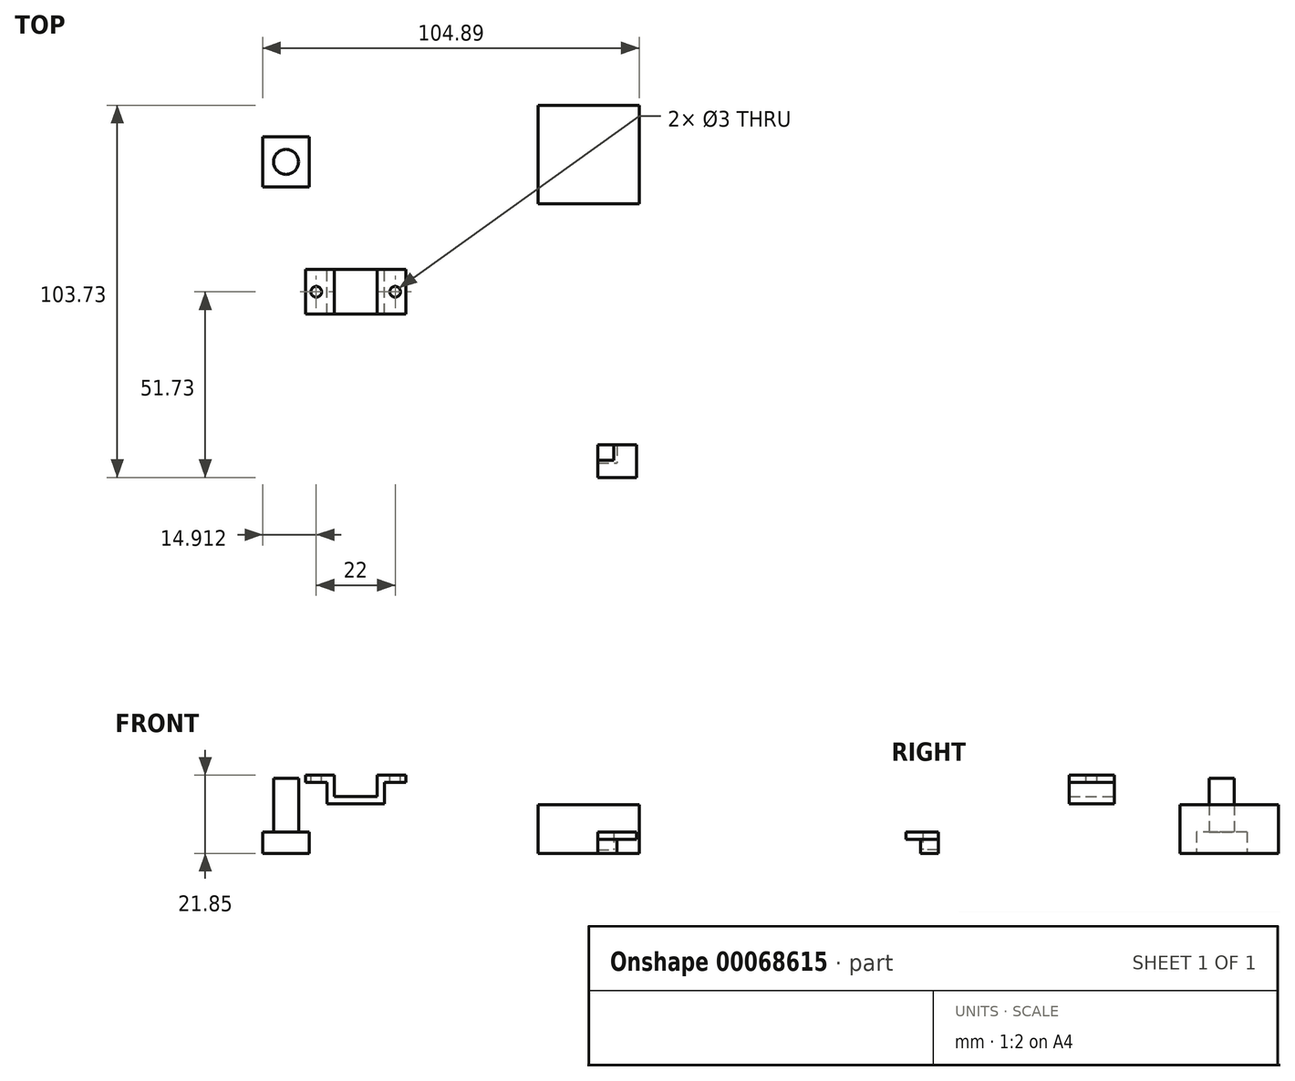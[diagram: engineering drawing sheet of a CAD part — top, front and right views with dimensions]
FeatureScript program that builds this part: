
annotation { "Feature Type Name" : "Feature", "Feature Type Description" : "" }
export const myFeature = defineFeature(function(context is Context, id is Id, definition is map)
    precondition{}
    {
        {
            var Q0;
            Q0=qCreatedBy(makeId("Front.planeOp"),FACE);
            var sketch = newSketch(context, id + "F0", { "sketchPlane" : qUnion([Q0])});
            skLineSegment(sketch, "E0", {"start": v(-31.6, 15.85) * mm, "end": v(-19.6, 15.85) * mm});
            skLineSegment(sketch, "E1", {"start": v(-19.6, 15.85) * mm, "end": v(-19.6, 21.85) * mm});
            skLineSegment(sketch, "E2", {"start": v(-19.6, 21.85) * mm, "end": v(-11.6, 21.85) * mm});
            skLineSegment(sketch, "E3", {"start": v(-11.6, 21.85) * mm, "end": v(-11.6, 19.85) * mm});
            skLineSegment(sketch, "E4", {"start": v(-11.6, 19.85) * mm, "end": v(-17.6, 19.85) * mm});
            skLineSegment(sketch, "E5", {"start": v(-17.6, 19.85) * mm, "end": v(-17.6, 13.85) * mm});
            skLineSegment(sketch, "E6", {"start": v(-17.6, 13.85) * mm, "end": v(-33.6, 13.85) * mm});
            skLineSegment(sketch, "E7", {"start": v(-33.6, 13.85) * mm, "end": v(-33.6, 19.85) * mm});
            skLineSegment(sketch, "E8", {"start": v(-33.6, 19.85) * mm, "end": v(-39.6, 19.85) * mm});
            skLineSegment(sketch, "E9", {"start": v(-39.6, 19.85) * mm, "end": v(-39.6, 21.85) * mm});
            skLineSegment(sketch, "E10", {"start": v(-39.6, 21.85) * mm, "end": v(-31.6, 21.85) * mm});
            skLineSegment(sketch, "E11", {"start": v(-31.6, 21.85) * mm, "end": v(-31.6, 15.85) * mm});
            skSolve(sketch);
        }
        {
            var Q0;
            Q0 = qSketchRegion(id + "F0", true);
            extrude(context, id + "F1", {"entities" : qUnion([Q0]), "depth" : 12.5 * mm});
        }
        {
            var Q0;
            Q0=makeQuery(id+"F1.opExtrude","CAP_FACE",FACE,{"disambiguationData":[OSD([sQuery(id+"F0.wireOp",EDGE,"E0"),sQuery(id+"F0.wireOp",EDGE,"E1"),sQuery(id+"F0.wireOp",EDGE,"E2"),sQuery(id+"F0.wireOp",EDGE,"E3"),sQuery(id+"F0.wireOp",EDGE,"E4"),sQuery(id+"F0.wireOp",EDGE,"E5"),sQuery(id+"F0.wireOp",EDGE,"E6"),sQuery(id+"F0.wireOp",EDGE,"E7"),sQuery(id+"F0.wireOp",EDGE,"E8"),sQuery(id+"F0.wireOp",EDGE,"E9"),sQuery(id+"F0.wireOp",EDGE,"E10"),sQuery(id+"F0.wireOp",EDGE,"E11")])],"isStart":false});
            cPlane(context, id + "F2", {"entities" : qUnion([Q0]), "cplaneType" : CPlaneType.OFFSET, "offset" : 2 * mm, "width" : 150 * mm, "height" : 150 * mm});
        }
        {
            var Q0;
            Q0=makeQuery(id+"F1.opExtrude","SWEPT_FACE",FACE,{"disambiguationData":[OSD([sQuery(id+"F0.wireOp",EDGE,"E10")])]});
            var sketch = newSketch(context, id + "F3", { "sketchPlane" : qUnion([Q0])});
            skCircle(sketch, "E12", {"center": v(-36.6, -6.25) * mm, "radius": 1.5 * mm});
            skCircle(sketch, "E13", {"center": v(-14.6, -6.25) * mm, "radius": 1.5 * mm});
            skSolve(sketch);
        }
        {
            var Q0;
            Q0 = qSketchRegion(id + "F3", true);
            extrude(context, id + "F4", {"entities" : qUnion([Q0]), "operationType" : NewBodyOperationType.REMOVE, "oppositeDirection" : true, "depth" : 2 * mm});
        }
        {
            var Q0;
            Q0=qCreatedBy(makeId("Top.planeOp"),FACE);
            var sketch = newSketch(context, id + "F5", { "sketchPlane" : qUnion([Q0])});
            skLineSegment(sketch, "E14.bottom", {"start": v(-51.52, 36.97) * mm, "end": v(-38.52, 36.97) * mm});
            skLineSegment(sketch, "E14.top", {"start": v(-51.52, 22.97) * mm, "end": v(-38.52, 22.97) * mm});
            skLineSegment(sketch, "E14.left", {"start": v(-51.52, 36.97) * mm, "end": v(-51.52, 22.97) * mm});
            skLineSegment(sketch, "E14.right", {"start": v(-38.52, 36.97) * mm, "end": v(-38.52, 22.97) * mm});
            skSolve(sketch);
        }
        {
            var Q0;
            Q0 = qSketchRegion(id + "F5", true);
            extrude(context, id + "F6", {"entities" : qUnion([Q0]), "depth" : 6 * mm});
        }
        {
            var Q0;
            Q0=makeQuery(id+"F6.opExtrude","CAP_FACE",FACE,{"disambiguationData":[OSD([sQuery(id+"F5.wireOp",EDGE,"E14.bottom"),sQuery(id+"F5.wireOp",EDGE,"E14.top"),sQuery(id+"F5.wireOp",EDGE,"E14.left"),sQuery(id+"F5.wireOp",EDGE,"E14.right")])],"isStart":false});
            var sketch = newSketch(context, id + "F7", { "sketchPlane" : qUnion([Q0])});
            skCircle(sketch, "E15", {"center": v(-45.02, 29.97) * mm, "radius": 3.5 * mm});
            skSolve(sketch);
        }
        {
            var Q0;
            Q0 = qSketchRegion(id + "F7", true);
            extrude(context, id + "F8", {"entities" : qUnion([Q0]), "operationType" : NewBodyOperationType.ADD, "depth" : 15 * mm});
        }
        {
            var Q0;
            Q0=qCreatedBy(makeId("Top.planeOp"),FACE);
            var sketch = newSketch(context, id + "F9", { "sketchPlane" : qUnion([Q0])});
            skLineSegment(sketch, "E16.bottom", {"start": v(41.85, -48.95) * mm, "end": v(47.23, -48.95) * mm});
            skLineSegment(sketch, "E16.top", {"start": v(41.85, -53.96) * mm, "end": v(47.23, -53.96) * mm});
            skLineSegment(sketch, "E16.left", {"start": v(41.85, -48.95) * mm, "end": v(41.85, -53.96) * mm});
            skLineSegment(sketch, "E16.right", {"start": v(47.23, -48.95) * mm, "end": v(47.23, -53.96) * mm});
            skSolve(sketch);
        }
        {
            var Q0;
            Q0 = qSketchRegion(id + "F9", true);
            extrude(context, id + "F10", {"entities" : qUnion([Q0]), "depth" : 1 * mm});
        }
        {
            var Q0;
            Q0=makeQuery(id+"F10.opExtrude","CAP_FACE",FACE,{"disambiguationData":[OSD([sQuery(id+"F9.wireOp",EDGE,"E16.bottom"),sQuery(id+"F9.wireOp",EDGE,"E16.top"),sQuery(id+"F9.wireOp",EDGE,"E16.left"),sQuery(id+"F9.wireOp",EDGE,"E16.right")])],"isStart":false});
            var sketch = newSketch(context, id + "F11", { "sketchPlane" : qUnion([Q0])});
            skLineSegment(sketch, "E17.bottom", {"start": v(46.24, -48.95) * mm, "end": v(47.23, -48.95) * mm});
            skLineSegment(sketch, "E17.top", {"start": v(41.85, -53.96) * mm, "end": v(47.23, -53.96) * mm});
            skLineSegment(sketch, "E17.left", {"start": v(41.85, -53.28) * mm, "end": v(41.85, -53.96) * mm});
            skLineSegment(sketch, "E17.right", {"start": v(47.23, -48.95) * mm, "end": v(47.23, -53.96) * mm});
            skLineSegment(sketch, "E18.top", {"start": v(41.85, -53.28) * mm, "end": v(46.24, -53.28) * mm});
            skLineSegment(sketch, "E18.right", {"start": v(46.24, -48.95) * mm, "end": v(46.24, -53.28) * mm});
            skSolve(sketch);
        }
        {
            var Q0;
            Q0 = qSketchRegion(id + "F11", true);
            extrude(context, id + "F12", {"entities" : qUnion([Q0]), "operationType" : NewBodyOperationType.ADD, "depth" : 5 * mm});
        }
        {
            var Q0;
            Q0=makeQuery(id+"F12.opExtrude","CAP_FACE",FACE,{"disambiguationData":[OSD([sQuery(id+"F11.wireOp",EDGE,"E17.bottom"),sQuery(id+"F11.wireOp",EDGE,"E17.top"),sQuery(id+"F11.wireOp",EDGE,"E17.left"),sQuery(id+"F11.wireOp",EDGE,"E17.right"),sQuery(id+"F11.wireOp",EDGE,"E18.top"),sQuery(id+"F11.wireOp",EDGE,"E18.right")])],"isStart":false});
            cPlane(context, id + "F13", {"entities" : qUnion([Q0]), "cplaneType" : CPlaneType.OFFSET, "offset" : 2 * mm, "oppositeDirection" : true, "width" : 150 * mm, "height" : 150 * mm});
        }
        {
            var Q0;
            Q0=qCreatedBy(id+"F13.planeOp",FACE);
            var sketch = newSketch(context, id + "F14", { "sketchPlane" : qUnion([Q0])});
            skLineSegment(sketch, "E19.bottom", {"start": v(47.23, -48.95) * mm, "end": v(52.67, -48.95) * mm});
            skLineSegment(sketch, "E19.top", {"start": v(41.85, -57.98) * mm, "end": v(52.67, -57.98) * mm});
            skLineSegment(sketch, "E19.left", {"start": v(41.85, -53.96) * mm, "end": v(41.85, -57.98) * mm});
            skLineSegment(sketch, "E19.right", {"start": v(52.67, -48.95) * mm, "end": v(52.67, -57.98) * mm});
            skLineSegment(sketch, "E20.top", {"start": v(41.85, -53.96) * mm, "end": v(47.23, -53.96) * mm});
            skLineSegment(sketch, "E20.right", {"start": v(47.23, -48.95) * mm, "end": v(47.23, -53.96) * mm});
            skSolve(sketch);
        }
        {
            var Q0;
            Q0 = qSketchRegion(id + "F14", true);
            extrude(context, id + "F15", {"entities" : qUnion([Q0]), "operationType" : NewBodyOperationType.ADD, "depth" : 2 * mm});
        }
        {
            var Q0;
            Q0=qCreatedBy(makeId("Top.planeOp"),FACE);
            var sketch = newSketch(context, id + "F16", { "sketchPlane" : qUnion([Q0])});
            skLineSegment(sketch, "E21.bottom", {"start": v(25.13, 45.75) * mm, "end": v(53.37, 45.75) * mm});
            skLineSegment(sketch, "E21.top", {"start": v(25.13, 18.3) * mm, "end": v(53.37, 18.3) * mm});
            skLineSegment(sketch, "E21.left", {"start": v(25.13, 45.75) * mm, "end": v(25.13, 18.3) * mm});
            skLineSegment(sketch, "E21.right", {"start": v(53.37, 45.75) * mm, "end": v(53.37, 18.3) * mm});
            skSolve(sketch);
        }
        {
            var Q0;
            Q0 = qSketchRegion(id + "F16", true);
            extrude(context, id + "F17", {"entities" : qUnion([Q0]), "depth" : 13.66 * mm});
        }
    });
